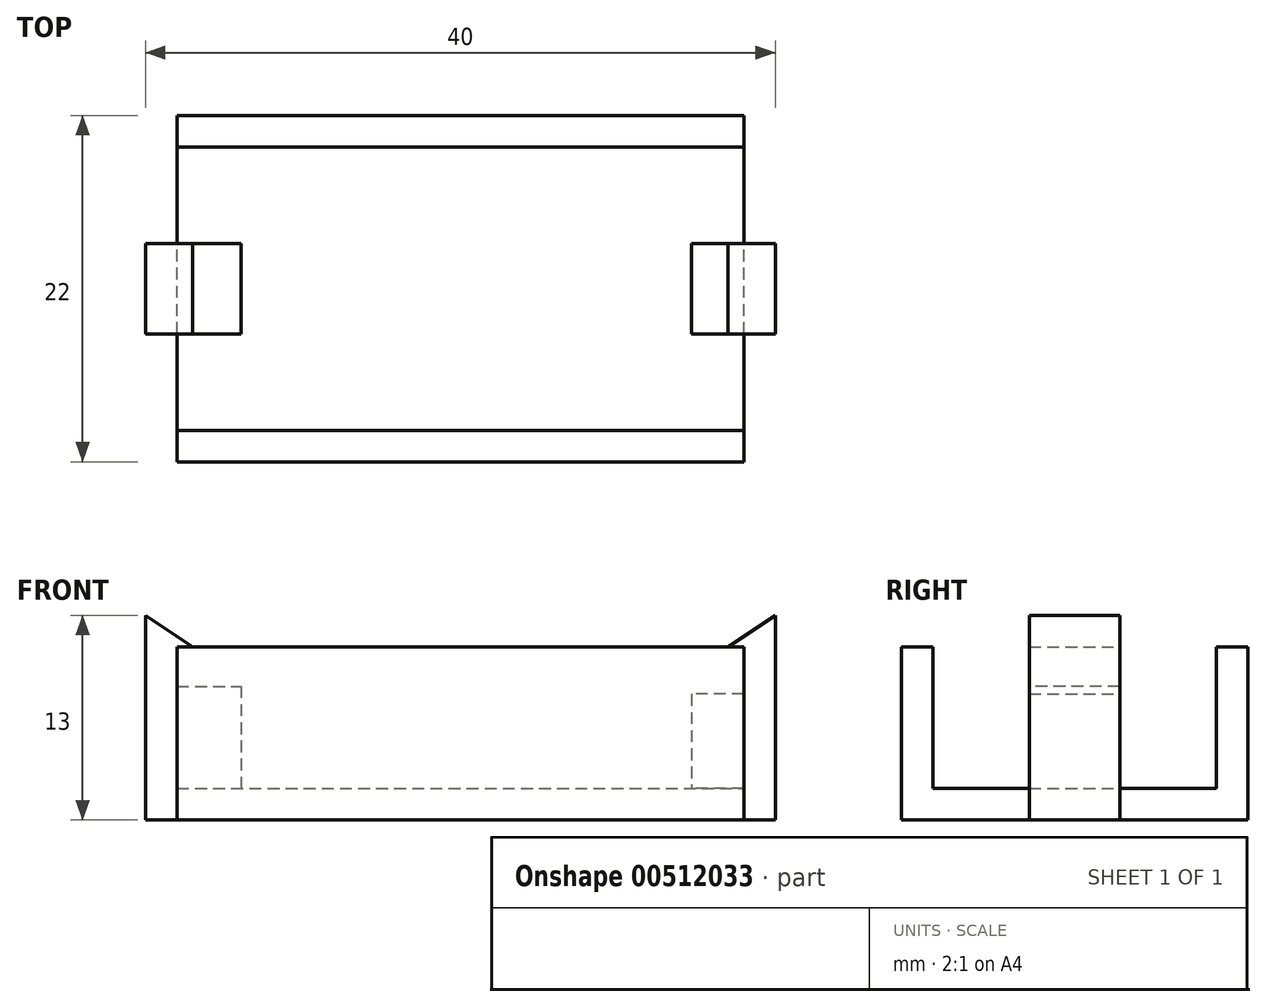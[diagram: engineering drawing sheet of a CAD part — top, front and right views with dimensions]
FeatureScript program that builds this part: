
annotation { "Feature Type Name" : "Feature", "Feature Type Description" : "" }
export const myFeature = defineFeature(function(context is Context, id is Id, definition is map)
    precondition{}
    {
        {
            var Q0;
            Q0=qCreatedBy(makeId("Top.planeOp"),FACE);
            var sketch = newSketch(context, id + "F0", { "sketchPlane" : qUnion([Q0])});
            skLineSegment(sketch, "E0.bottom", {"start": v(18, -9) * mm, "end": v(-18, -9) * mm});
            skLineSegment(sketch, "E0.top", {"start": v(18, 9) * mm, "end": v(-18, 9) * mm});
            skLineSegment(sketch, "E0.left", {"start": v(18, -9) * mm, "end": v(18, 9) * mm});
            skLineSegment(sketch, "E0.right", {"start": v(-18, -9) * mm, "end": v(-18, 9) * mm});
            skPoint(sketch, "E0.middle", {"position": v(0, 0) * mm});
            skLineSegment(sketch, "E1.bottom", {"start": v(-18, 11) * mm, "end": v(18, 11) * mm});
            skLineSegment(sketch, "E1.top", {"start": v(-18, -11) * mm, "end": v(18, -11) * mm});
            skLineSegment(sketch, "E1.left", {"start": v(-18, 11) * mm, "end": v(-18, -11) * mm});
            skLineSegment(sketch, "E1.right", {"start": v(18, 11) * mm, "end": v(18, -11) * mm});
            skLineSegment(sketch, "E2.bottom", {"start": v(-18, 2.87) * mm, "end": v(-13.92, 2.87) * mm});
            skLineSegment(sketch, "E2.top", {"start": v(-18, -2.87) * mm, "end": v(-13.92, -2.87) * mm});
            skLineSegment(sketch, "E2.left", {"start": v(-18, 2.87) * mm, "end": v(-18, -2.87) * mm});
            skLineSegment(sketch, "E2.right", {"start": v(-13.92, 2.87) * mm, "end": v(-13.92, -2.87) * mm});
            skPoint(sketch, "E3.firstSnap0", {"position": v(18, 0) * mm});
            skPoint(sketch, "E3.oppositeSnap0", {"position": v(-15.96, 2.87) * mm});
            skLineSegment(sketch, "E3.bottom", {"start": v(18, -2.87) * mm, "end": v(14.7, -2.87) * mm});
            skLineSegment(sketch, "E3.top", {"start": v(18, 2.87) * mm, "end": v(14.7, 2.87) * mm});
            skLineSegment(sketch, "E3.left", {"start": v(18, -2.87) * mm, "end": v(18, 2.87) * mm});
            skLineSegment(sketch, "E3.right", {"start": v(14.7, -2.87) * mm, "end": v(14.7, 2.87) * mm});
            skLineSegment(sketch, "E4", {"start": v(-18, 9) * mm, "end": v(-18, 9) * mm});
            skLineSegment(sketch, "E5", {"start": v(-18, -9) * mm, "end": v(-18, -9) * mm});
            skLineSegment(sketch, "E6", {"start": v(18, -9) * mm, "end": v(18, -9) * mm});
            skLineSegment(sketch, "E7", {"start": v(18, 9) * mm, "end": v(18, 9) * mm});
            skPoint(sketch, "E8.oppositeSnap0", {"position": v(-15.96, -2.87) * mm});
            skLineSegment(sketch, "E8.bottom", {"start": v(-18, 2.87) * mm, "end": v(-20, 2.87) * mm});
            skLineSegment(sketch, "E8.top", {"start": v(-18, -2.87) * mm, "end": v(-20, -2.87) * mm});
            skLineSegment(sketch, "E8.right", {"start": v(-20, 2.87) * mm, "end": v(-20, -2.87) * mm});
            skLineSegment(sketch, "E9.bottom", {"start": v(18, 2.87) * mm, "end": v(20, 2.87) * mm});
            skLineSegment(sketch, "E9.top", {"start": v(18, -2.87) * mm, "end": v(20, -2.87) * mm});
            skLineSegment(sketch, "E9.left", {"start": v(18, 2.87) * mm, "end": v(18, -2.87) * mm});
            skLineSegment(sketch, "E9.right", {"start": v(20, 2.87) * mm, "end": v(20, -2.87) * mm});
            skSolve(sketch);
        }
        {
            var Q0;
            Q0=makeQuery(id+"F0.imprint","IMPRINT",FACE,{"disambiguationData":[TD([[makeQuery(id+"F0.imprint","IMPRINT",EDGE,{"derivedFrom":sQuery(id+"F0.wireOp",EDGE,"E0.bottom")}),1.0]])]});
            var Q1;
            Q1=makeQuery(id+"F0.imprint","IMPRINT",FACE,{"disambiguationData":[TD([[makeQuery(id+"F0.imprint","IMPRINT",EDGE,{"derivedFrom":sQuery(id+"F0.wireOp",EDGE,"E0.bottom")}),-1.0]])]});
            extrude(context, id + "F1", {"entities" : qUnion([Q0, Q1]), "depth" : 2 * mm, "offsetDistance" : 25 * mm});
        }
        {
            var Q0;
            Q0=makeQuery(id+"F0.imprint","IMPRINT",FACE,{"disambiguationData":[TD([[makeQuery(id+"F0.imprint","IMPRINT",EDGE,{"derivedFrom":sQuery(id+"F0.wireOp",EDGE,"E2.bottom")}),-1.0]])]});
            extrude(context, id + "F2", {"entities" : qUnion([Q0]), "operationType" : NewBodyOperationType.ADD, "depth" : 8.5 * mm, "offsetDistance" : 25 * mm});
        }
        {
            var Q0;
            {var subQ3=sQuery(id+"F0.wireOp",EDGE,"E0.bottom");Q0=makeQuery(id+"F0.imprint","IMPRINT",FACE,{"disambiguationData":[TD([[makeQuery(id+"F0.imprint","IMPRINT",EDGE,{"derivedFrom":subQ3}),1.0]])]});}
            var Q1;
            {var subQ0=sQuery(id+"F0.wireOp",EDGE,"E0.top");Q1=makeQuery(id+"F0.imprint","IMPRINT",FACE,{"disambiguationData":[TD([[makeQuery(id+"F0.imprint","IMPRINT",EDGE,{"derivedFrom":subQ0}),-1.0]])]});}
            extrude(context, id + "F3", {"entities" : qUnion([Q0, Q1]), "operationType" : NewBodyOperationType.ADD, "depth" : 11 * mm, "offsetDistance" : 25 * mm});
        }
        {
            var Q0;
            Q0=makeQuery(id+"F0.imprint","IMPRINT",FACE,{"disambiguationData":[TD([[makeQuery(id+"F0.imprint","IMPRINT",EDGE,{"derivedFrom":sQuery(id+"F0.wireOp",EDGE,"E8.bottom")}),1.0]])]});
            var Q1;
            Q1=makeQuery(id+"F0.imprint","IMPRINT",FACE,{"disambiguationData":[TD([[makeQuery(id+"F0.imprint","IMPRINT",EDGE,{"derivedFrom":sQuery(id+"F0.wireOp",EDGE,"E9.bottom")}),-1.0]])]});
            extrude(context, id + "F4", {"entities" : qUnion([Q0, Q1]), "operationType" : NewBodyOperationType.ADD, "depth" : 11 * mm, "offsetDistance" : 25 * mm});
        }
        {
            var Q0;
            Q0=makeQuery(id+"F4.opExtrude","CAP_FACE",FACE,{"disambiguationData":[OSD([sQuery(id+"F0.wireOp",EDGE,"E8.bottom"),sQuery(id+"F0.wireOp",EDGE,"E8.top"),sQuery(id+"F0.wireOp",EDGE,"E2.left"),sQuery(id+"F0.wireOp",EDGE,"E8.right")])],"isStart":false});
            var sketch = newSketch(context, id + "F5", { "sketchPlane" : qUnion([Q0])});
            skLineSegment(sketch, "E10.bottom", {"start": v(-20, 2.87) * mm, "end": v(-17, 2.87) * mm});
            skLineSegment(sketch, "E10.top", {"start": v(-20, -2.87) * mm, "end": v(-17, -2.87) * mm});
            skLineSegment(sketch, "E10.left", {"start": v(-20, 2.87) * mm, "end": v(-20, -2.87) * mm});
            skLineSegment(sketch, "E10.right", {"start": v(-17, 2.87) * mm, "end": v(-17, -2.87) * mm});
            skLineSegment(sketch, "E11.bottom", {"start": v(20, 2.87) * mm, "end": v(17, 2.87) * mm});
            skLineSegment(sketch, "E11.top", {"start": v(20, -2.87) * mm, "end": v(17, -2.87) * mm});
            skLineSegment(sketch, "E11.left", {"start": v(20, 2.87) * mm, "end": v(20, -2.87) * mm});
            skLineSegment(sketch, "E11.right", {"start": v(17, 2.87) * mm, "end": v(17, -2.87) * mm});
            skSolve(sketch);
        }
        {
            var Q0;
            Q0=makeQuery(id+"F5.imprint","IMPRINT",FACE,{"disambiguationData":[TD([[makeQuery(id+"F5.imprint","IMPRINT",EDGE,{"derivedFrom":sQuery(id+"F5.wireOp",EDGE,"E11.bottom")}),1.0]])]});
            var Q1;
            {var subQ2=sQuery(id+"F5.wireOp",EDGE,"E10.left");Q1=makeQuery(id+"F5.imprint","IMPRINT",FACE,{"disambiguationData":[TD([[makeQuery(id+"F5.imprint","IMPRINT",EDGE,{"derivedFrom":subQ2}),1.0]])]});}
            var Q2;
            {var subQ2=sQuery(id+"F5.wireOp",EDGE,"E10.right");Q2=makeQuery(id+"F5.imprint","IMPRINT",FACE,{"disambiguationData":[TD([[makeQuery(id+"F5.imprint","IMPRINT",EDGE,{"derivedFrom":subQ2}),-1.0]])]});}
            extrude(context, id + "F6", {"entities" : qUnion([Q0, Q1, Q2]), "operationType" : NewBodyOperationType.ADD, "depth" : 2 * mm, "offsetDistance" : 25 * mm});
        }
        {
            var Q0;
            Q0=makeQuery(id+"F6.boolean.opBoolean","MERGE",FACE,{"derivedFrom":[makeQuery(id+"F4.boolean.opBoolean","MERGE",FACE,{"derivedFrom":[makeQuery(id+"F2.opExtrude","SWEPT_FACE",FACE,{"disambiguationData":[OSD([sQuery(id+"F0.wireOp",EDGE,"E2.top")])]}),makeQuery(id+"F4.opExtrude","SWEPT_FACE",FACE,{"disambiguationData":[OSD([sQuery(id+"F0.wireOp",EDGE,"E8.top")])]})]}),makeQuery(id+"F6.opExtrude","SWEPT_FACE",FACE,{"disambiguationData":[OSD([sQuery(id+"F5.wireOp",EDGE,"E10.top")])]})]});
            var sketch = newSketch(context, id + "F7", { "sketchPlane" : qUnion([Q0])});
            skLineSegment(sketch, "E12", {"start": v(-17, 11) * mm, "end": v(-20, 13) * mm});
            skSolve(sketch);
        }
        {
            var Q0;
            Q0=makeQuery(id+"F7.imprint","IMPRINT",FACE,{"disambiguationData":[TD([[makeQuery(id+"F7.imprint","IMPRINT",EDGE,{"derivedFrom":sQuery(id+"F7.wireOp",EDGE,"E12")}),-1.0]])]});
            extrude(context, id + "F8", {"entities" : qUnion([Q0]), "operationType" : NewBodyOperationType.REMOVE, "endBound" : BoundingType.UP_TO_NEXT, "oppositeDirection" : true, "depth" : 25 * mm, "offsetDistance" : 25 * mm});
        }
        {
            var Q0;
            Q0=makeQuery(id+"F6.boolean.opBoolean","MERGE",FACE,{"derivedFrom":[makeQuery(id+"F4.boolean.opBoolean","MERGE",FACE,{"derivedFrom":[makeQuery(id+"F2.opExtrude","SWEPT_FACE",FACE,{"disambiguationData":[OSD([sQuery(id+"F0.wireOp",EDGE,"E3.bottom")])]}),makeQuery(id+"F4.opExtrude","SWEPT_FACE",FACE,{"disambiguationData":[OSD([sQuery(id+"F0.wireOp",EDGE,"E9.top")])]})]}),makeQuery(id+"F6.opExtrude","SWEPT_FACE",FACE,{"disambiguationData":[OSD([sQuery(id+"F5.wireOp",EDGE,"E11.top")])]})]});
            var sketch = newSketch(context, id + "F9", { "sketchPlane" : qUnion([Q0])});
            skLineSegment(sketch, "E13", {"start": v(17, 11) * mm, "end": v(20, 13) * mm});
            skSolve(sketch);
        }
        {
            var Q0;
            {var subQ0=sQuery(id+"F9.wireOp",EDGE,"OlgT4jq8-CX8n-xrEq-LsZK-j39kxfpaLJ2W");Q0=makeQuery(id+"F9.imprint","IMPRINT",FACE,{"disambiguationData":[TD([[makeQuery(id+"F9.imprint","IMPRINT",EDGE,{"derivedFrom":subQ0}),1.0]])]});}
            var Q1;
            Q1=makeQuery(id+"F9.imprint","IMPRINT",FACE,{"disambiguationData":[TD([[makeQuery(id+"F9.imprint","IMPRINT",EDGE,{"derivedFrom":sQuery(id+"F9.wireOp",EDGE,"E13")}),1.0]])]});
            extrude(context, id + "F10", {"entities" : qUnion([Q0, Q1]), "operationType" : NewBodyOperationType.REMOVE, "endBound" : BoundingType.UP_TO_NEXT, "oppositeDirection" : true, "depth" : 25 * mm, "offsetDistance" : 25 * mm});
        }
        {
            var Q0;
            Q0=makeQuery(id+"F0.imprint","IMPRINT",FACE,{"disambiguationData":[TD([[makeQuery(id+"F0.imprint","IMPRINT",EDGE,{"derivedFrom":sQuery(id+"F0.wireOp",EDGE,"E3.bottom")}),-1.0]])]});
            extrude(context, id + "F11", {"entities" : qUnion([Q0]), "operationType" : NewBodyOperationType.ADD, "depth" : 8 * mm, "offsetDistance" : 25 * mm});
        }
    });
